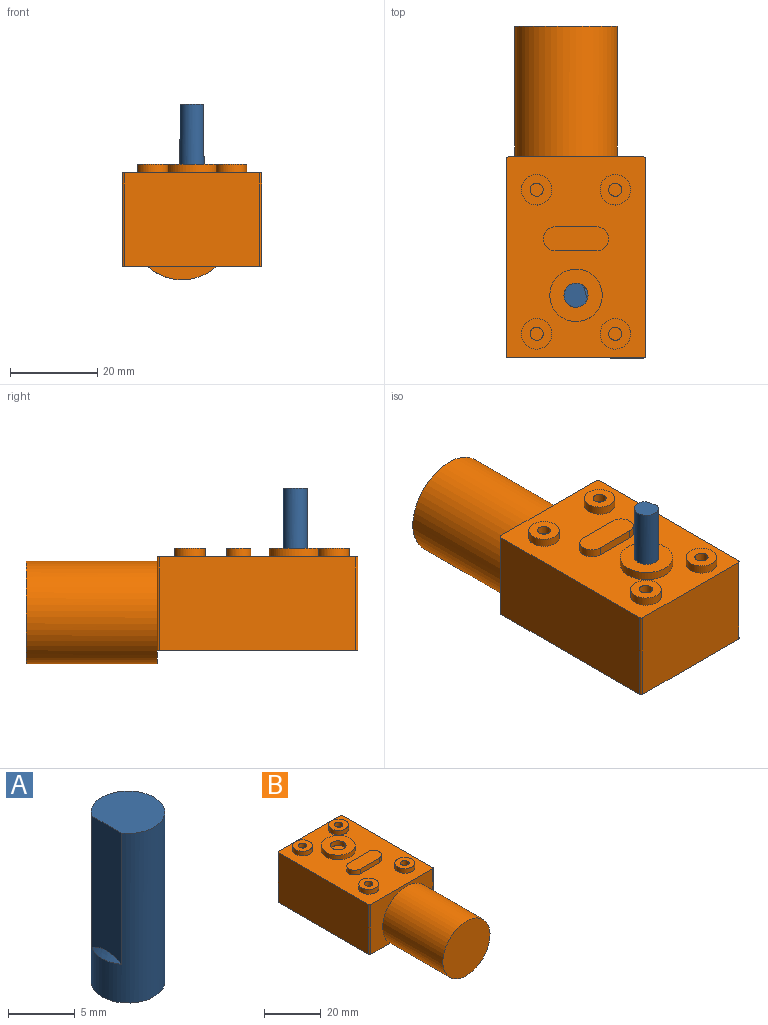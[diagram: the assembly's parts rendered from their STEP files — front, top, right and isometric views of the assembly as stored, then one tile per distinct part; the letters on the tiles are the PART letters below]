
ASSEMBLY  parts=2 mates=1
PART A: 5 faces, bbox 5.5x5.5x15.5 mm
  f0: plane 12x3.16mm, normal (-1,0,0), area 36.9mm2, adj f1,f2,f4
  f1: cylinder r=2.75mm len=15.5mm, axis (0,0,-1), area 227.4mm2, adj f0,f2,f3,f4
  f2: plane 5.5x5mm, normal (0,0,1), area 22.7mm2, adj f0,f1
  f3: plane 5.5x5.5mm, normal (0,0,-1), area 23.8mm2, adj f1
  f4: cone r=2.25mm half-angle=45deg, axis (0,0,-1), area 1.5mm2, adj f0,f1
PART B: 38 faces, bbox 32x76x26.5 mm
  f0: plane 46x32mm, normal (0,0,1), area 1128.7mm2, adj f1,f2,f3,f4,f5,f6,f7,f8
  f1: plane 31x21.5mm, normal (0,1,0), area 666.5mm2, adj f0,f2,f8,f9
  f2: cylinder r=0.5mm len=21.5mm, axis (0,0,1), area 16.9mm2, adj f0,f1,f3,f9
  f3: plane 45x21.5mm, normal (-1,0,0), area 967.5mm2, adj f0,f2,f4,f9
  f4: cylinder r=0.5mm len=21.5mm, axis (0,0,1), area 16.9mm2, adj f0,f3,f5,f9
  f5: plane 31x21.5mm, normal (0,-1,0), area 265mm2, adj f0,f4,f6,f9,f36
  f6: cylinder r=0.5mm len=21.5mm, axis (0,0,1), area 16.9mm2, adj f0,f5,f7,f9
  f7: plane 45x21.5mm, normal (1,0,0), area 967.5mm2, adj f0,f6,f8,f9
  f8: cylinder r=0.5mm len=21.5mm, axis (0,0,1), area 16.9mm2, adj f0,f1,f7,f9
  f9: plane 46x32mm, normal (0,0,-1), area 1471.8mm2, adj f1,f2,f3,f4,f5,f6,f7,f8
  f10: cylinder r=1.5mm len=3mm, axis (0,0,-1), area 18.8mm2, adj f12,f13
  f11: cylinder r=3.5mm len=7mm, axis (0,0,-1), area 44mm2, adj f0,f12
  f12: plane 7x7mm, normal (0,0,1), area 31.4mm2, adj f10,f11
  f13: plane 3x3mm, normal (0,0,1), area 7.1mm2, adj f10
  f14: cylinder r=1.5mm len=3mm, axis (0,0,-1), area 18.8mm2, adj f16,f17
  f15: cylinder r=3.5mm len=7mm, axis (0,0,-1), area 44mm2, adj f0,f16
  f16: plane 7x7mm, normal (0,0,1), area 31.4mm2, adj f14,f15
  f17: plane 3x3mm, normal (0,0,1), area 7.1mm2, adj f14
  f18: cylinder r=1.5mm len=3mm, axis (0,0,-1), area 18.8mm2, adj f20,f21
  f19: cylinder r=3.5mm len=7mm, axis (0,0,-1), area 44mm2, adj f0,f20
  f20: plane 7x7mm, normal (0,0,1), area 31.4mm2, adj f18,f19
  f21: plane 3x3mm, normal (0,0,1), area 7.1mm2, adj f18
  f22: cylinder r=1.5mm len=3mm, axis (0,0,-1), area 18.8mm2, adj f24,f25
  f23: cylinder r=3.5mm len=7mm, axis (0,0,-1), area 44mm2, adj f0,f24
  f24: plane 7x7mm, normal (0,0,1), area 31.4mm2, adj f22,f23
  f25: plane 3x3mm, normal (0,0,1), area 7.1mm2, adj f22
  f26: cylinder r=2.75mm len=5.5mm, axis (0,0,-1), area 34.6mm2, adj f28,f29
  f27: cylinder r=6mm len=12mm, axis (0,0,-1), area 75.4mm2, adj f0,f28
  f28: plane 12x12mm, normal (0,0,1), area 89.3mm2, adj f26,f27
  f29: plane 5.5x5.5mm, normal (0,0,1), area 23.8mm2, adj f26
  f30: plane 9.5x2mm, normal (0,1,0), area 19mm2, adj f0,f31,f33,f34
  f31: cylinder r=2.75mm len=5.5mm, axis (0,0,-1), area 17.3mm2, adj f0,f30,f32,f34
  f32: plane 9.5x2mm, normal (0,-1,0), area 19mm2, adj f0,f31,f33,f34
  f33: cylinder r=2.75mm len=5.5mm, axis (0,0,-1), area 17.3mm2, adj f0,f30,f32,f34
  f34: plane 15x5.5mm, normal (0,0,1), area 76mm2, adj f30,f31,f32,f33
  f35: plane 15.68x3mm, normal (0,1,0), area 32.3mm2, adj f9,f36
  f36: cylinder r=11.75mm len=30mm, axis (0,1,0), area 2214.8mm2, adj f5,f35,f37
  f37: plane 23.5x23.5mm, normal (0,-1,0), area 433.7mm2, adj f36
PLACE A rot(axis=(0,0,-1),165deg) t=(24.51,-16.74,19.24)mm
PLACE B rot(axis=(0,0,1),180deg) t=(24.51,-16.74,18.99)mm
MATE cylindrical B.f26 <-> A.f1  axis (0,0,-1) through (24.51,-16.74,19.99)mm
